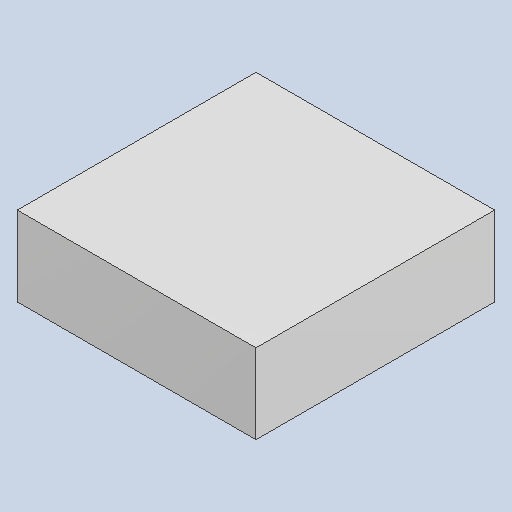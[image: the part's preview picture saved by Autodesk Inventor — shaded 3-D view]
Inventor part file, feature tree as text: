
AUTODESK INVENTOR PART (.ipt)
format: ipt  version: 2023.4 (Build 274418000, 418)  size: 79,872 bytes
history: native  units: mm
features: extrude x1
ambient origin geometry x8: Origin, YZ Plane, XZ Plane, XY Plane, X Axis, Y Axis, Z Axis, Center Point
bodies: Solid1 (feature_tree)
feature tree (1):
  extrude  "Extruded_41"  [1 undecoded]
note: 1 required parameter value undecoded (feature->parameter linkage not recoverable at this tier; creation-order binding heuristic only, values carry confidence <= 0.55)
